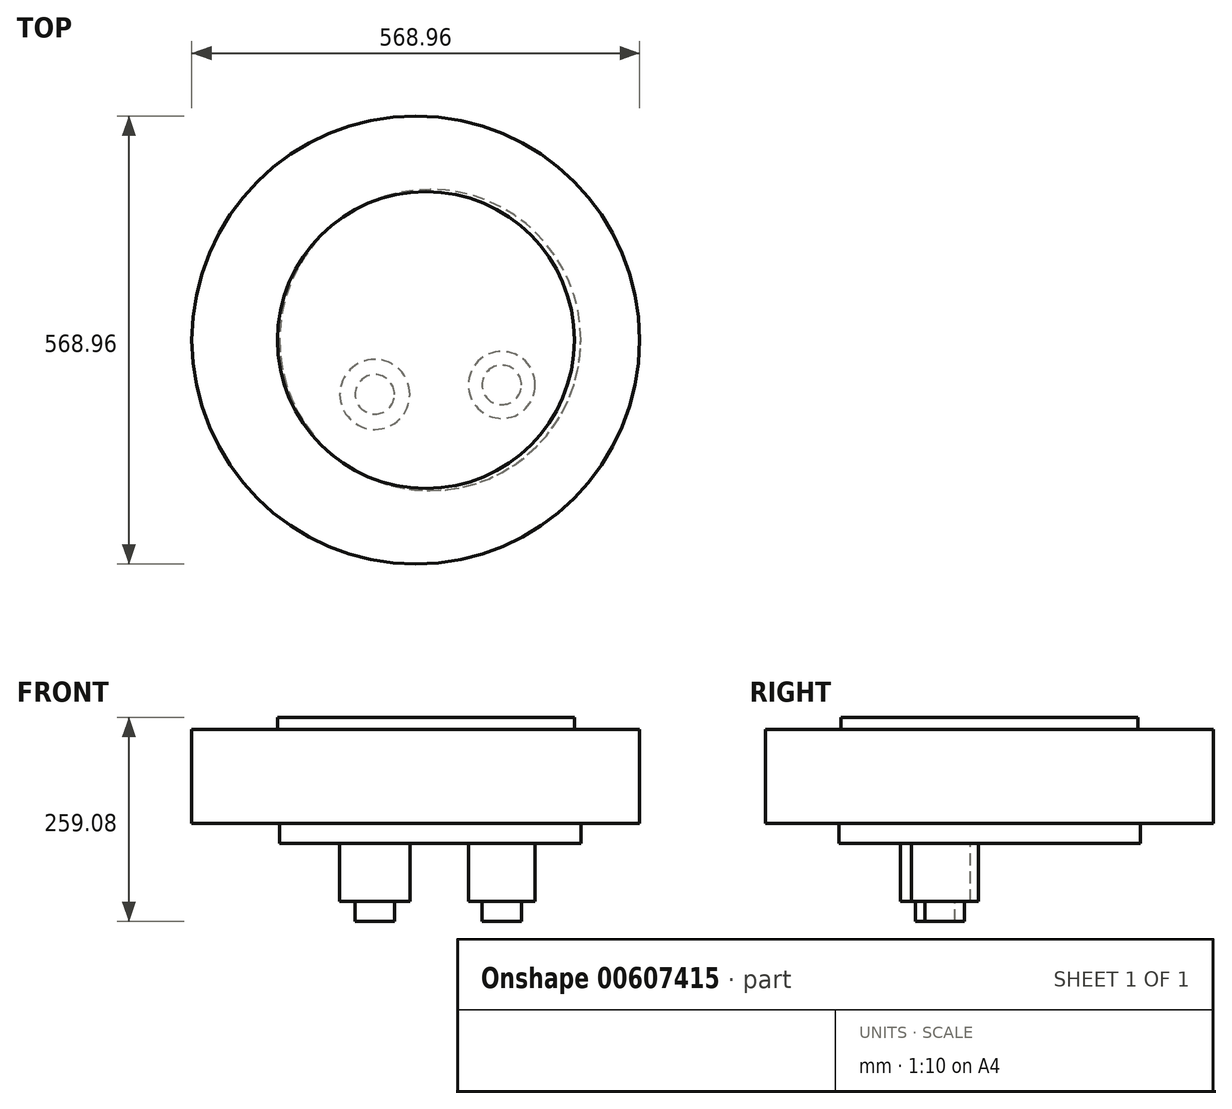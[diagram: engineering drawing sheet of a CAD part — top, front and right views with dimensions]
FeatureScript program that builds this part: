
annotation { "Feature Type Name" : "Feature", "Feature Type Description" : "" }
export const myFeature = defineFeature(function(context is Context, id is Id, definition is map)
    precondition{}
    {
        {
            var Q0;
            Q0=qCreatedBy(makeId("Top.planeOp"),FACE);
            var sketch = newSketch(context, id + "F0", { "sketchPlane" : qUnion([Q0])});
            skCircle(sketch, "E0", {"center": v(0, 0) * mm, "radius": 284.48 * mm});
            skCircle(sketch, "E1", {"center": v(127.08, 0) * mm, "radius": 113.56 * mm});
            skCircle(sketch, "E2", {"center": v(-138, 0) * mm, "radius": 107.2 * mm});
            skArc(sketch, "E3", {"start": v(94.8, 158.06) * mm, "mid": v(-10.4, 205) * mm, "end": v(-102.77, 136.17) * mm});
            skArc(sketch, "E4", {"start": v(94.8, 158.06) * mm, "mid": v(-4.08, 148) * mm, "end": v(-102.77, 136.17) * mm});
            skSolve(sketch);
        }
        {
            var Q0;
            Q0 = qSketchRegion(id + "F0", true);
            var Q1;
            Q1=makeQuery(id+"F0.imprint","IMPRINT",FACE,{"disambiguationData":[TD([[makeQuery(id+"F0.imprint","IMPRINT",EDGE,{"derivedFrom":sQuery(id+"F0.wireOp",EDGE,"E2")}),1.0]])]});
            var Q2;
            Q2=makeQuery(id+"F0.imprint","IMPRINT",FACE,{"disambiguationData":[TD([[makeQuery(id+"F0.imprint","IMPRINT",EDGE,{"derivedFrom":sQuery(id+"F0.wireOp",EDGE,"E1")}),1.0]])]});
            var Q3;
            Q3=makeQuery(id+"F0.imprint","IMPRINT",FACE,{"disambiguationData":[TD([[makeQuery(id+"F0.imprint","IMPRINT",EDGE,{"derivedFrom":sQuery(id+"F0.wireOp",EDGE,"E3")}),1.0]])]});
            extrude(context, id + "F1", {"entities" : qUnion([Q0, Q1, Q2, Q3]), "depth" : 43.18 * mm, "offsetDistance" : 25.4 * mm});
        }
        {
            var Q0;
            Q0=makeQuery(id+"F1.opExtrude","CAP_FACE",FACE,{"disambiguationData":[OSD([sQuery(id+"F0.wireOp",EDGE,"E0")])],"isStart":true});
            extrude(context, id + "F2", {"entities" : qUnion([Q0]), "operationType" : NewBodyOperationType.ADD, "depth" : 25.4 * mm, "offsetDistance" : 25.4 * mm});
        }
        {
            var Q0;
            Q0=makeQuery(id+"F2.opExtrude","CAP_FACE",FACE,{"disambiguationData":[OSD([sQuery(id+"F0.wireOp",EDGE,"E0")])],"isStart":false});
            var sketch = newSketch(context, id + "F3", { "sketchPlane" : qUnion([Q0])});
            skCircle(sketch, "E5", {"center": v(12.94, 0) * mm, "radius": 188.58 * mm});
            skSolve(sketch);
        }
        {
            var Q0;
            Q0 = qSketchRegion(id + "F3", true);
            extrude(context, id + "F4", {"entities" : qUnion([Q0]), "operationType" : NewBodyOperationType.ADD, "oppositeDirection" : true, "depth" : 83.82 * mm, "offsetDistance" : 25.4 * mm});
        }
        {
            var Q0;
            Q0=makeQuery(id+"F2.opExtrude","CAP_FACE",FACE,{"disambiguationData":[OSD([sQuery(id+"F0.wireOp",EDGE,"E0")])],"isStart":false});
            var sketch = newSketch(context, id + "F5", { "sketchPlane" : qUnion([Q0])});
            skCircle(sketch, "E6", {"center": v(18.28, 0) * mm, "radius": 191.3 * mm});
            skSolve(sketch);
        }
        {
            var Q0;
            Q0 = qSketchRegion(id + "F5", true);
            extrude(context, id + "F6", {"entities" : qUnion([Q0]), "operationType" : NewBodyOperationType.ADD, "depth" : 25.4 * mm, "offsetDistance" : 25.4 * mm});
        }
        {
            var Q0;
            Q0=makeQuery(id+"F2.opExtrude","CAP_FACE",FACE,{"disambiguationData":[OSD([sQuery(id+"F0.wireOp",EDGE,"E0")])],"isStart":false});
            var Q1;
            Q1=makeQuery(id+"F6.opExtrude","CAP_FACE",FACE,{"disambiguationData":[OSD([sQuery(id+"F5.wireOp",EDGE,"E6")])],"isStart":false});
            extrude(context, id + "F7", {"entities" : qUnion([Q0, Q1]), "operationType" : NewBodyOperationType.ADD, "depth" : 50.8 * mm, "offsetDistance" : 25.4 * mm});
        }
        {
            var Q0;
            Q0=makeQuery(id+"F7.opExtrude","CAP_FACE",FACE,{"disambiguationData":[OSD([sQuery(id+"F5.wireOp",EDGE,"E6")])],"isStart":false});
            var sketch = newSketch(context, id + "F8", { "sketchPlane" : qUnion([Q0])});
            skCircle(sketch, "E7", {"center": v(-52.02, 69.08) * mm, "radius": 44.49 * mm});
            skCircle(sketch, "E8", {"center": v(109.22, 57.05) * mm, "radius": 42.51 * mm});
            skArc(sketch, "E9", {"start": v(-62.69, -53.65) * mm, "mid": v(25.03, -112) * mm, "end": v(121.05, -68.63) * mm});
            skSolve(sketch);
        }
        {
            var Q0;
            Q0 = qSketchRegion(id + "F8", true);
            extrude(context, id + "F9", {"entities" : qUnion([Q0]), "operationType" : NewBodyOperationType.ADD, "depth" : 73.66 * mm, "offsetDistance" : 25.4 * mm});
        }
        {
            var Q0;
            Q0=makeQuery(id+"F7.opExtrude","CAP_FACE",FACE,{"disambiguationData":[OSD([sQuery(id+"F5.wireOp",EDGE,"E6")])],"isStart":false});
            var sketch = newSketch(context, id + "F10", { "sketchPlane" : qUnion([Q0])});
            skArc(sketch, "E10", {"start": v(-63.93, -56.53) * mm, "mid": v(21.36, -115.85) * mm, "end": v(114.1, -69.03) * mm});
            skSolve(sketch);
        }
        {
            var Q0;
            Q0=makeQuery(id+"F9.opExtrude","CAP_FACE",FACE,{"disambiguationData":[OSD([sQuery(id+"F8.wireOp",EDGE,"E7")])],"isStart":false});
            var sketch = newSketch(context, id + "F11", { "sketchPlane" : qUnion([Q0])});
            skCircle(sketch, "E11", {"center": v(-52.02, 69.08) * mm, "radius": 25.06 * mm});
            skSolve(sketch);
        }
        {
            var Q0;
            Q0 = qSketchRegion(id + "F11", true);
            extrude(context, id + "F12", {"entities" : qUnion([Q0]), "operationType" : NewBodyOperationType.ADD, "oppositeDirection" : true, "depth" : 96.52 * mm, "offsetDistance" : 25.4 * mm});
        }
        {
            var Q0;
            Q0=makeQuery(id+"F9.opExtrude","CAP_FACE",FACE,{"disambiguationData":[OSD([sQuery(id+"F8.wireOp",EDGE,"E7")])],"isStart":false});
            var sketch = newSketch(context, id + "F13", { "sketchPlane" : qUnion([Q0])});
            skCircle(sketch, "E12", {"center": v(-52.02, 69.08) * mm, "radius": 24.54 * mm});
            skSolve(sketch);
        }
        {
            var Q0;
            Q0=makeQuery(id+"F9.opExtrude","CAP_FACE",FACE,{"disambiguationData":[OSD([sQuery(id+"F8.wireOp",EDGE,"E8")])],"isStart":false});
            var sketch = newSketch(context, id + "F14", { "sketchPlane" : qUnion([Q0])});
            skCircle(sketch, "E13", {"center": v(109.22, 57.05) * mm, "radius": 25.05 * mm});
            skSolve(sketch);
        }
        {
            var Q0;
            Q0=makeQuery(id+"F13.imprint","IMPRINT",FACE,{"disambiguationData":[TD([[makeQuery(id+"F13.imprint","IMPRINT",EDGE,{"derivedFrom":sQuery(id+"F13.wireOp",EDGE,"E12")}),1.0]])]});
            extrude(context, id + "F15", {"entities" : qUnion([Q0]), "operationType" : NewBodyOperationType.ADD, "oppositeDirection" : true, "depth" : 60.96 * mm, "offsetDistance" : 25.4 * mm});
        }
        {
            var Q0;
            Q0=makeQuery(id+"F14.imprint","IMPRINT",FACE,{"disambiguationData":[TD([[makeQuery(id+"F14.imprint","IMPRINT",EDGE,{"derivedFrom":sQuery(id+"F14.wireOp",EDGE,"E13")}),1.0]])]});
            var sketch = newSketch(context, id + "F16", { "sketchPlane" : qUnion([Q0])});
            skSolve(sketch);
        }
        {
            var Q0;
            Q0=makeQuery(id+"F16.imprint","IMPRINT",FACE,{"disambiguationData":[TD([[makeQuery(id+"F16.imprint","IMPRINT",EDGE,{"derivedFrom":makeQuery(id+"F14.imprint","IMPRINT",EDGE,{"derivedFrom":sQuery(id+"F14.wireOp",EDGE,"E13")})}),1.0]])]});
            extrude(context, id + "F17", {"entities" : qUnion([Q0]), "operationType" : NewBodyOperationType.ADD, "depth" : 25.4 * mm, "offsetDistance" : 25.4 * mm});
        }
        {
            var Q0;
            Q0=makeQuery(id+"F9.opExtrude","CAP_FACE",FACE,{"disambiguationData":[OSD([sQuery(id+"F8.wireOp",EDGE,"E7")])],"isStart":false});
            var sketch = newSketch(context, id + "F18", { "sketchPlane" : qUnion([Q0])});
            skCircle(sketch, "E14", {"center": v(-52.02, 69.08) * mm, "radius": 25.06 * mm});
            skSolve(sketch);
        }
        {
            var Q0;
            Q0=makeQuery(id+"F18.imprint","IMPRINT",FACE,{"disambiguationData":[TD([[makeQuery(id+"F18.imprint","IMPRINT",EDGE,{"derivedFrom":sQuery(id+"F18.wireOp",EDGE,"E14")}),1.0]])]});
            extrude(context, id + "F19", {"entities" : qUnion([Q0]), "operationType" : NewBodyOperationType.ADD, "depth" : 25.4 * mm, "offsetDistance" : 25.4 * mm});
        }
        {
            var Q0;
            Q0 = qConstructionFilter(qBodyType(qCreatedBy(id + "F10" ,EDGE), BodyType.WIRE), ConstructionObject.NO);
            extrude(context, id + "F20", {"bodyType" : ToolBodyType.SURFACE, "surfaceEntities" : qUnion([Q0]), "depth" : 50.8 * mm, "offsetDistance" : 25.4 * mm});
        }
    });
